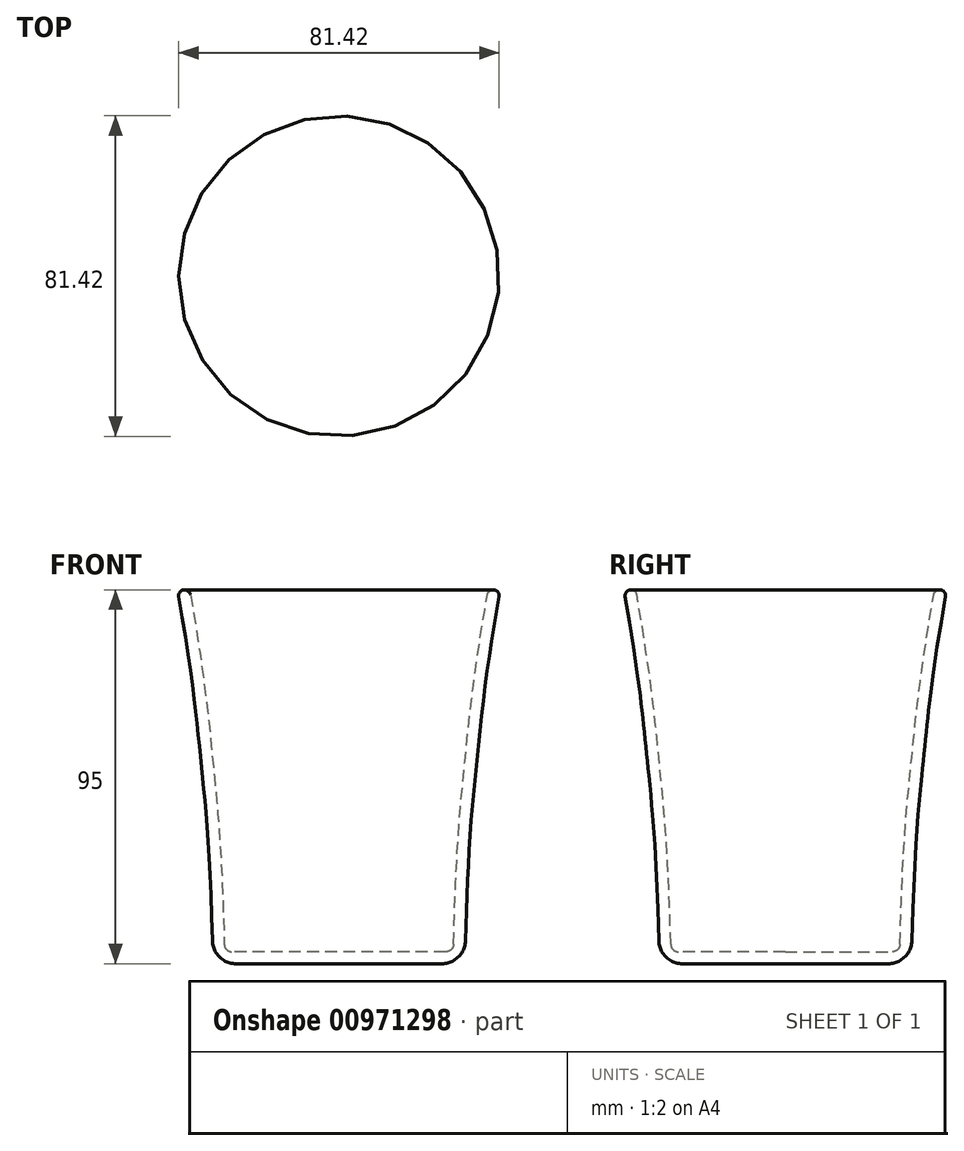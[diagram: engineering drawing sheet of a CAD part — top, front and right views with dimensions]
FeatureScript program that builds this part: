
annotation { "Feature Type Name" : "Feature", "Feature Type Description" : "" }
export const myFeature = defineFeature(function(context is Context, id is Id, definition is map)
    precondition{}
    {
        {
            var Q0;
            Q0=qCreatedBy(makeId("Front.planeOp"),FACE);
            var sketch = newSketch(context, id + "F0", { "sketchPlane" : qUnion([Q0])});
            skLineSegment(sketch, "E0", {"start": v(32, 0) * mm, "end": v(0, 0) * mm});
            skLineSegment(sketch, "E1", {"start": v(0, 0) * mm, "end": v(0, 95) * mm});
            skLineSegment(sketch, "E2", {"start": v(0, 95) * mm, "end": v(41, 95) * mm});
            skFitSpline(sketch, "E3", {"points": [v(41, 95) * mm, v(35.1, 52.02) * mm, v(32, 0) * mm], "startDerivative": vector(-24.55, -138.35) * mm, "endDerivative": vector(-3.72, -169.86) * mm});
            skSolve(sketch);
        }
        {
            var Q0;
            Q0=makeQuery(id+"F0.imprint","IMPRINT",FACE,{"disambiguationData":[TD([[makeQuery(id+"F0.imprint","IMPRINT",EDGE,{"derivedFrom":sQuery(id+"F0.wireOp",EDGE,"E0")}),-1.0]])]});
            var Q1;
            Q1=sQuery(id+"F0.wireOp",EDGE,"E1");
            revolve(context, id + "F1", {"surfaceOperationType" : NewSurfaceOperationType.NEW, "entities" : qUnion([Q0]), "axis" : qUnion([Q1]), "revolveType" : RevolveType.FULL});
        }
        {
            var Q0;
            Q0=makeQuery(id+"F1.opRevolve","SWEPT_FACE",FACE,{"disambiguationData":[OSD([sQuery(id+"F0.wireOp",EDGE,"E2")])]});
            shell(context, id + "F2", {"entities" : qUnion([Q0]), "thickness" : 3 * mm});
        }
        {
            var Q0;
            Q0=makeQuery(id+"F1.opRevolve","SWEPT_EDGE",EDGE,{"disambiguationData":[OSD([sQuery(id+"F0.wireOp",EDGE,"E2"),sQuery(id+"F0.wireOp",EDGE,"E3")])]});
            var Q1;
            Q1=makeQuery(id+"F2.opShell","OFFSET_EDGE",EDGE,{"disambiguationData":[OSD([sQuery(id+"F0.wireOp",EDGE,"E2"),sQuery(id+"F0.wireOp",EDGE,"E3")])]});
            fillet(context, id + "F3", {"entities" : qUnion([Q0, Q1]), "radius" : 1.5 * mm, "tangentPropagation" : true, "allowEdgeOverflow" : false});
        }
        {
            var Q0;
            Q0=makeQuery(id+"F1.opRevolve","SWEPT_EDGE",EDGE,{"disambiguationData":[OSD([sQuery(id+"F0.wireOp",EDGE,"E0"),sQuery(id+"F0.wireOp",EDGE,"E3")])]});
            fillet(context, id + "F4", {"entities" : qUnion([Q0]), "radius" : 6 * mm, "tangentPropagation" : true, "allowEdgeOverflow" : false});
        }
        {
            var Q0;
            Q0=makeQuery(id+"F2.opShell","OFFSET_EDGE",EDGE,{"disambiguationData":[OSD([sQuery(id+"F0.wireOp",EDGE,"E0"),sQuery(id+"F0.wireOp",EDGE,"E3")])]});
            fillet(context, id + "F5", {"entities" : qUnion([Q0]), "radius" : 2 * mm, "tangentPropagation" : true, "allowEdgeOverflow" : false});
        }
    });
